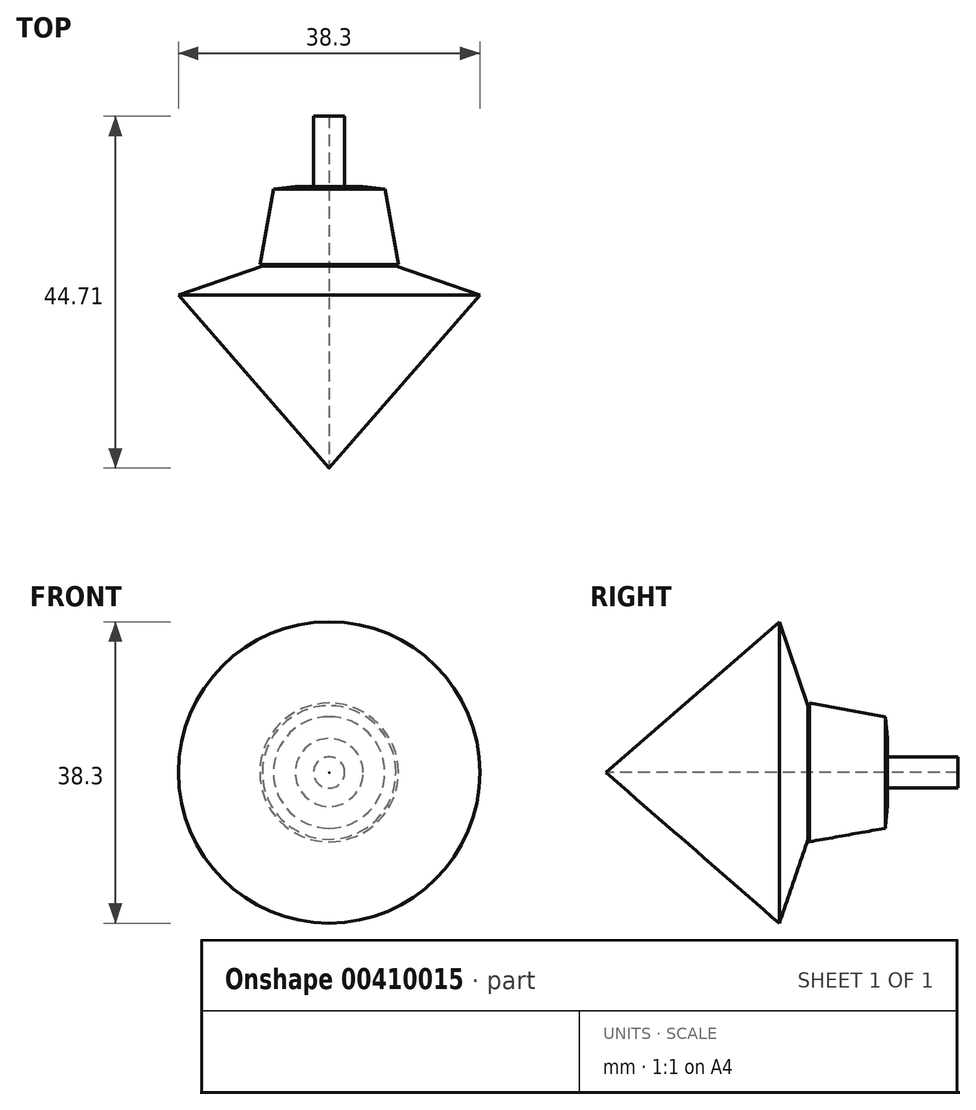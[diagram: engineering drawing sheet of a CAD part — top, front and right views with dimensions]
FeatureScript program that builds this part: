
annotation { "Feature Type Name" : "Feature", "Feature Type Description" : "" }
export const myFeature = defineFeature(function(context is Context, id is Id, definition is map)
    precondition{}
    {
        {
            var Q0;
            Q0=qCreatedBy(makeId("Top.planeOp"),FACE);
            var sketch = newSketch(context, id + "F0", { "sketchPlane" : qUnion([Q0])});
            skLineSegment(sketch, "E0", {"start": v(0, -31.15) * mm, "end": v(0, 53.97) * mm});
            skLineSegment(sketch, "E1", {"start": v(0, 53.97) * mm, "end": v(0, -31.15) * mm});
            skLineSegment(sketch, "E2", {"start": v(0, -31.15) * mm, "end": v(19.15, -9.13) * mm});
            skLineSegment(sketch, "E3", {"start": v(19.15, -9.13) * mm, "end": v(8.48, -5.45) * mm});
            skLineSegment(sketch, "E4", {"start": v(8.48, -5.45) * mm, "end": v(25.4, 2.64) * mm});
            skLineSegment(sketch, "E5", {"start": v(25.4, 2.64) * mm, "end": v(4.31, 4.6) * mm});
            skLineSegment(sketch, "E6", {"start": v(4.31, 4.6) * mm, "end": v(1.98, 4.6) * mm});
            skLineSegment(sketch, "E7", {"start": v(1.98, 4.6) * mm, "end": v(1.98, 13.56) * mm});
            skLineSegment(sketch, "E8", {"start": v(1.98, 13.56) * mm, "end": v(0, 13.56) * mm});
            skLineSegment(sketch, "E9", {"start": v(0, 13.56) * mm, "end": v(0, -31.15) * mm});
            skSolve(sketch);
        }
        {
            var Q0;
            Q0=sQuery(id+"F0.wireOp",EDGE,"E5");
            var Q1;
            Q1=sQuery(id+"F0.wireOp",EDGE,"E7");
            var Q2;
            Q2=sQuery(id+"F0.wireOp",EDGE,"E4");
            var Q3;
            Q3=sQuery(id+"F0.wireOp",EDGE,"E3");
            var Q4;
            Q4=sQuery(id+"F0.wireOp",EDGE,"E2");
            var Q5;
            Q5=sQuery(id+"F0.wireOp",EDGE,"E9");
            var Q6;
            Q6=sQuery(id+"F0.wireOp",EDGE,"E8");
            var Q7;
            Q7=sQuery(id+"F0.wireOp",EDGE,"E6");
            var Q8;
            Q8=sQuery(id+"F0.wireOp",EDGE,"E1");
            revolve(context, id + "F1", {"bodyType" : ToolBodyType.SURFACE, "surfaceEntities" : qUnion([Q0, Q1, Q2, Q3, Q4, Q5, Q6, Q7]), "axis" : qUnion([Q8]), "revolveType" : RevolveType.FULL});
        }
        {
            var Q0;
            Q0=makeQuery(id+"F1.opRevolve","SWEPT_EDGE",EDGE,{"disambiguationData":[OSD([sQuery(id+"F0.wireOp",VERTEX,"E4.end")])]});
            chamfer(context, id + "F2", {"entities" : qUnion([Q0]), "width" : 5.08 * mm, "tangentPropagation" : true});
        }
    });
